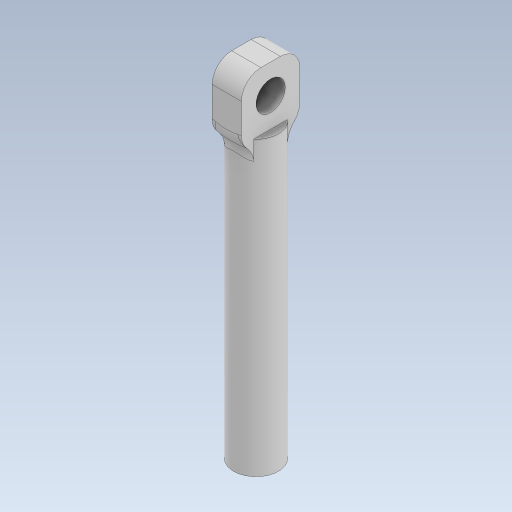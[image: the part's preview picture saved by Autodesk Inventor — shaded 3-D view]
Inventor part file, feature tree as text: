
AUTODESK INVENTOR PART (.ipt)
format: ipt  version: 2023.5 (Build 275446000, 446)  size: 190,976 bytes
history: native  units: mm
features: extrude x3, sketch x2, fillet x1
ambient origin geometry x8: Origin, YZ Plane, XZ Plane, XY Plane, X Axis, Y Axis, Z Axis, Center Point
bodies: Solid1 (feature_tree)
feature tree (6):
  sketch  "Sketch1"  dims[d0=4.6mm d1=6.0mm d2=0.0mm]
  extrude  "Extrusion1"  Depth=6.0mm TaperAngle=0.0deg
  extrude  "Extrusion2"  Depth=3.0mm
  extrude  "Extrusion3"  Depth=20.0mm TaperAngle=0.0deg
  fillet  "Fillet1"  Radius=2.0mm
  sketch  "Sketch2"  dims[d3=30.0mm d4=0.0mm d5=3.0mm d6=20.0mm d7=0.0mm d8=2.0mm d9=6.0mm d10=3.0mm]
